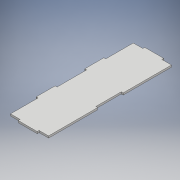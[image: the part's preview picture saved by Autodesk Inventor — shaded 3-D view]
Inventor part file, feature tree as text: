
AUTODESK INVENTOR PART (.ipt)
format: ipt  version: 2017 (Build 210142000, 142)  size: 137,216 bytes
history: native  units: mm
features: extrude x1, sketch x1
ambient origin geometry x8: Origin, YZ Plane, XZ Plane, XY Plane, X Axis, Y Axis, Z Axis, Center Point
bodies: Solid1 (feature_tree)
feature tree (2):
  extrude  "Extrusion1"  Depth=77.0mm
  sketch  "Sketch1"  dims[d23=3.0mm d24=0.0mm d25=193.0mm d26=60.0mm d27=3.0mm d28=30.0mm d29=15.0mm d30=3.0mm d31=3.0mm d32=15.0mm d33=3.0mm d34=3.0mm d35=3.0mm d36=3.0mm d37=15.0mm d38=40.0mm d39=3.0mm d41=77.0mm d43=3.0mm d44=76.0mm d45=199.145723mm d46=43.3mm d47=46.6mm d48=43.3mm d49=30.0mm d50=29.8mm]
